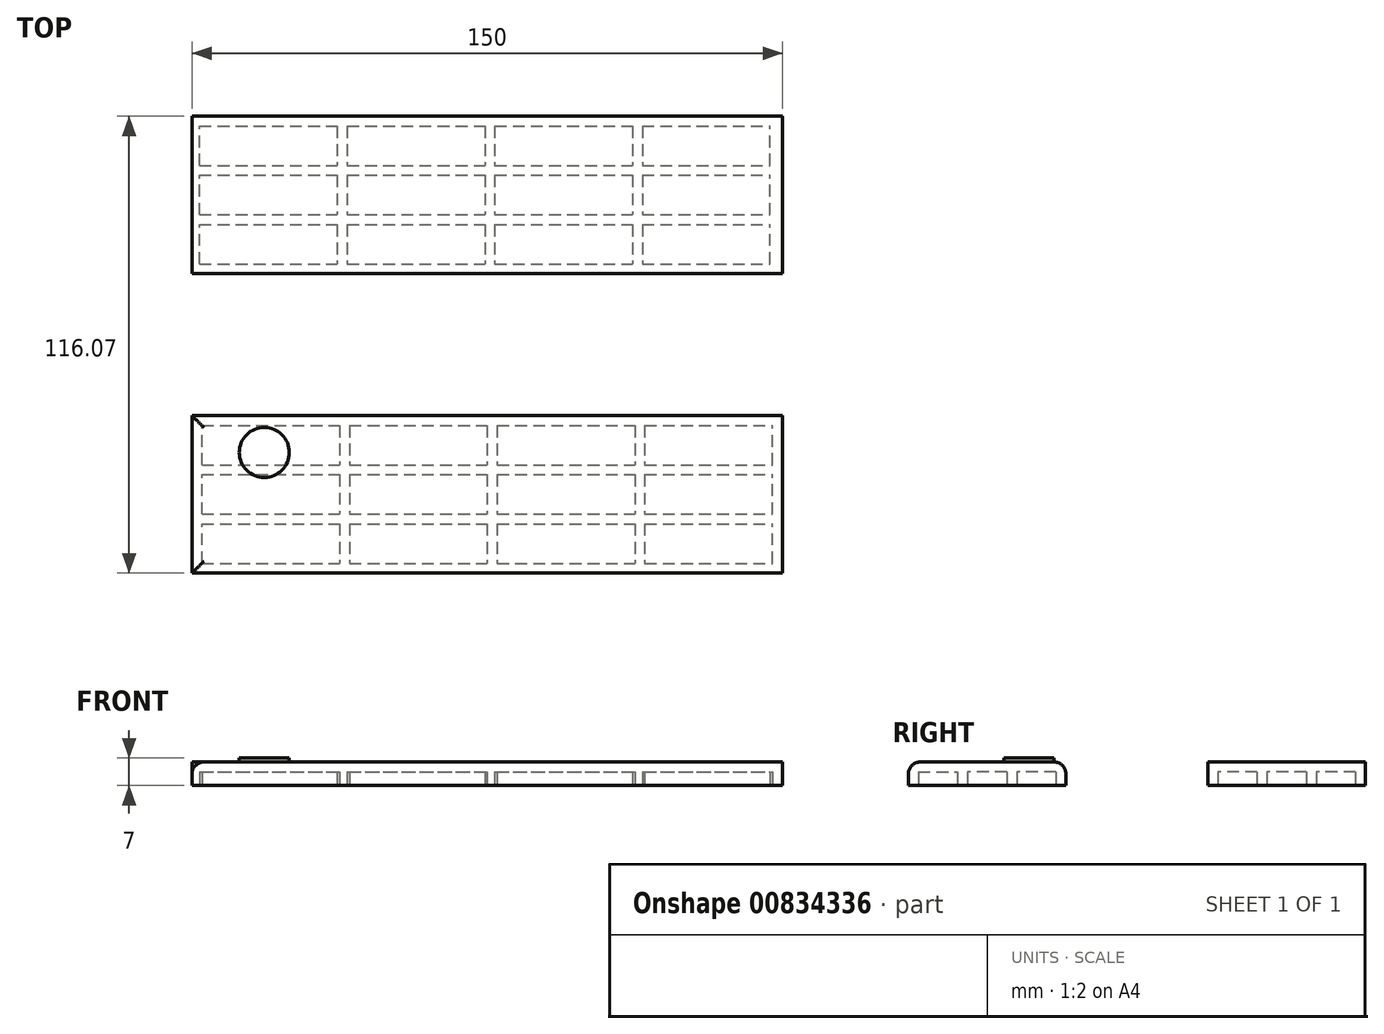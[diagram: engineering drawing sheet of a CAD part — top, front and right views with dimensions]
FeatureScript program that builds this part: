
annotation { "Feature Type Name" : "Feature", "Feature Type Description" : "" }
export const myFeature = defineFeature(function(context is Context, id is Id, definition is map)
    precondition{}
    {
        {
            var Q0;
            Q0=qCreatedBy(makeId("Top.planeOp"),FACE);
            var sketch = newSketch(context, id + "F0", { "sketchPlane" : qUnion([Q0])});
            skLineSegment(sketch, "E0.bottom", {"start": v(75, 20) * mm, "end": v(-75, 20) * mm});
            skLineSegment(sketch, "E0.top", {"start": v(75, -20) * mm, "end": v(-75, -20) * mm});
            skLineSegment(sketch, "E0.left", {"start": v(75, 20) * mm, "end": v(75, -20) * mm});
            skLineSegment(sketch, "E0.right", {"start": v(-75, 20) * mm, "end": v(-75, -20) * mm});
            skPoint(sketch, "E0.middle", {"position": v(0, 0) * mm});
            skSolve(sketch);
        }
        {
            var Q0;
            Q0 = qSketchRegion(id + "F0", true);
            extrude(context, id + "F1", {"entities" : qUnion([Q0]), "depth" : 6 * mm, "offsetDistance" : 25.4 * mm});
        }
        {
            var Q0;
            Q0=qCreatedBy(makeId("Top.planeOp"),FACE);
            var sketch = newSketch(context, id + "F2", { "sketchPlane" : qUnion([Q0])});
            skLineSegment(sketch, "E1.bottom", {"start": v(75, -56.07) * mm, "end": v(-75, -56.07) * mm});
            skLineSegment(sketch, "E1.top", {"start": v(75, -96.07) * mm, "end": v(-75, -96.07) * mm});
            skLineSegment(sketch, "E1.left", {"start": v(75, -56.07) * mm, "end": v(75, -96.07) * mm});
            skLineSegment(sketch, "E1.right", {"start": v(-75, -56.07) * mm, "end": v(-75, -96.07) * mm});
            skPoint(sketch, "E1.middle", {"position": v(0, -76.07) * mm});
            skSolve(sketch);
        }
        {
            var Q0;
            Q0 = qSketchRegion(id + "F2", true);
            extrude(context, id + "F3", {"entities" : qUnion([Q0]), "depth" : 6 * mm, "offsetDistance" : 25.4 * mm});
        }
        {
            var Q0;
            Q0=makeQuery(id+"F3.opExtrude","CAP_FACE",FACE,{"disambiguationData":[OSD([sQuery(id+"F2.wireOp",EDGE,"E1.bottom"),sQuery(id+"F2.wireOp",EDGE,"E1.top"),sQuery(id+"F2.wireOp",EDGE,"E1.left"),sQuery(id+"F2.wireOp",EDGE,"E1.right")])],"isStart":false});
            var sketch = newSketch(context, id + "F4", { "sketchPlane" : qUnion([Q0])});
            skCircle(sketch, "E2", {"center": v(-56.65, -65.42) * mm, "radius": 6.35 * mm});
            skSolve(sketch);
        }
        {
            var Q0;
            Q0 = qSketchRegion(id + "F4", true);
            extrude(context, id + "F5", {"entities" : qUnion([Q0]), "operationType" : NewBodyOperationType.ADD, "depth" : 1 * mm, "offsetDistance" : 25.4 * mm});
        }
        {
            var Q0;
            Q0=makeQuery(id+"F3.opExtrude","CAP_FACE",FACE,{"disambiguationData":[OSD([sQuery(id+"F2.wireOp",EDGE,"E1.bottom"),sQuery(id+"F2.wireOp",EDGE,"E1.top"),sQuery(id+"F2.wireOp",EDGE,"E1.left"),sQuery(id+"F2.wireOp",EDGE,"E1.right")])],"isStart":true});
            var sketch = newSketch(context, id + "F6", { "sketchPlane" : qUnion([Q0])});
            skLineSegment(sketch, "E3.bottom", {"start": v(-72.5, 93.57) * mm, "end": v(72.5, 93.57) * mm});
            skLineSegment(sketch, "E3.top", {"start": v(-72.5, 83.57) * mm, "end": v(72.5, 83.57) * mm});
            skLineSegment(sketch, "E3.left", {"start": v(-72.5, 93.57) * mm, "end": v(-72.5, 83.57) * mm});
            skLineSegment(sketch, "E3.right", {"start": v(72.5, 93.57) * mm, "end": v(72.5, 83.57) * mm});
            skLineSegment(sketch, "E4.bottom", {"start": v(-72.5, 81.07) * mm, "end": v(72.5, 81.07) * mm});
            skLineSegment(sketch, "E4.top", {"start": v(-72.5, 71.07) * mm, "end": v(72.5, 71.07) * mm});
            skLineSegment(sketch, "E4.left", {"start": v(-72.5, 81.07) * mm, "end": v(-72.5, 71.07) * mm});
            skLineSegment(sketch, "E4.right", {"start": v(72.5, 81.07) * mm, "end": v(72.5, 71.07) * mm});
            skLineSegment(sketch, "E5.bottom", {"start": v(-72.5, 68.57) * mm, "end": v(72.5, 68.57) * mm});
            skLineSegment(sketch, "E5.top", {"start": v(-72.5, 58.57) * mm, "end": v(72.5, 58.57) * mm});
            skLineSegment(sketch, "E5.left", {"start": v(-72.5, 68.57) * mm, "end": v(-72.5, 58.57) * mm});
            skLineSegment(sketch, "E5.right", {"start": v(72.5, 68.57) * mm, "end": v(72.5, 58.57) * mm});
            skLineSegment(sketch, "E6.bottom", {"start": v(-37.5, 58.57) * mm, "end": v(-35, 58.57) * mm});
            skLineSegment(sketch, "E6.top", {"start": v(-37.5, 93.57) * mm, "end": v(-35, 93.57) * mm});
            skLineSegment(sketch, "E6.left", {"start": v(-37.5, 58.57) * mm, "end": v(-37.5, 93.57) * mm});
            skLineSegment(sketch, "E6.right", {"start": v(-35, 58.57) * mm, "end": v(-35, 93.57) * mm});
            skLineSegment(sketch, "E7.bottom", {"start": v(0, 58.57) * mm, "end": v(2.5, 58.57) * mm});
            skLineSegment(sketch, "E7.top", {"start": v(0, 93.57) * mm, "end": v(2.5, 93.57) * mm});
            skLineSegment(sketch, "E7.left", {"start": v(0, 58.57) * mm, "end": v(0, 93.57) * mm});
            skLineSegment(sketch, "E7.right", {"start": v(2.5, 58.57) * mm, "end": v(2.5, 93.57) * mm});
            skLineSegment(sketch, "E8.bottom", {"start": v(37.5, 58.57) * mm, "end": v(40, 58.57) * mm});
            skLineSegment(sketch, "E8.top", {"start": v(37.5, 93.57) * mm, "end": v(40, 93.57) * mm});
            skLineSegment(sketch, "E8.left", {"start": v(37.5, 58.57) * mm, "end": v(37.5, 93.57) * mm});
            skLineSegment(sketch, "E8.right", {"start": v(40, 58.57) * mm, "end": v(40, 93.57) * mm});
            skSolve(sketch);
        }
        {
            var Q0;
            {var subQ0=sQuery(id+"F6.wireOp",EDGE,"E3.left");Q0=makeQuery(id+"F6.imprint","IMPRINT",FACE,{"disambiguationData":[TD([[makeQuery(id+"F6.imprint","IMPRINT",EDGE,{"derivedFrom":subQ0}),1.0]])]});}
            var Q1;
            {var subQ0=sQuery(id+"F6.wireOp",EDGE,"E6.right");var subQ5=sQuery(id+"F6.wireOp",EDGE,"E3.top");var subQ6=makeQuery(id+"F6.imprint","INTERSECT",VERTEX,{"derivedFrom":[subQ5,subQ0]});Q1=makeQuery(id+"F6.imprint","IMPRINT",FACE,{"disambiguationData":[TD([[makeQuery(id+"F6.imprint","IMPRINT",EDGE,{"disambiguationData":[TD([[subQ6,-1.0]])],"derivedFrom":subQ5}),1.0]])]});}
            var Q2;
            {var subQ0=sQuery(id+"F6.wireOp",EDGE,"E6.right");var subQ1=sQuery(id+"F6.wireOp",EDGE,"E4.bottom");var subQ2=makeQuery(id+"F6.imprint","INTERSECT",VERTEX,{"derivedFrom":[subQ1,subQ0]});Q2=makeQuery(id+"F6.imprint","IMPRINT",FACE,{"disambiguationData":[TD([[makeQuery(id+"F6.imprint","IMPRINT",EDGE,{"disambiguationData":[TD([[subQ2,-1.0]])],"derivedFrom":subQ1}),-1.0]])]});}
            var Q3;
            {var subQ0=sQuery(id+"F6.wireOp",EDGE,"E4.left");Q3=makeQuery(id+"F6.imprint","IMPRINT",FACE,{"disambiguationData":[TD([[makeQuery(id+"F6.imprint","IMPRINT",EDGE,{"derivedFrom":subQ0}),1.0]])]});}
            var Q4;
            {var subQ0=sQuery(id+"F6.wireOp",EDGE,"E5.left");Q4=makeQuery(id+"F6.imprint","IMPRINT",FACE,{"disambiguationData":[TD([[makeQuery(id+"F6.imprint","IMPRINT",EDGE,{"derivedFrom":subQ0}),1.0]])]});}
            var Q5;
            {var subQ0=sQuery(id+"F6.wireOp",EDGE,"E7.right");var subQ1=sQuery(id+"F6.wireOp",EDGE,"E5.bottom");var subQ2=makeQuery(id+"F6.imprint","INTERSECT",VERTEX,{"derivedFrom":[subQ1,subQ0]});Q5=makeQuery(id+"F6.imprint","IMPRINT",FACE,{"disambiguationData":[TD([[makeQuery(id+"F6.imprint","IMPRINT",EDGE,{"disambiguationData":[TD([[subQ2,-1.0]])],"derivedFrom":subQ1}),-1.0]])]});}
            var Q6;
            {var subQ0=sQuery(id+"F6.wireOp",EDGE,"E7.right");var subQ1=sQuery(id+"F6.wireOp",EDGE,"E4.bottom");var subQ2=makeQuery(id+"F6.imprint","INTERSECT",VERTEX,{"derivedFrom":[subQ1,subQ0]});Q6=makeQuery(id+"F6.imprint","IMPRINT",FACE,{"disambiguationData":[TD([[makeQuery(id+"F6.imprint","IMPRINT",EDGE,{"disambiguationData":[TD([[subQ2,-1.0]])],"derivedFrom":subQ1}),-1.0]])]});}
            var Q7;
            {var subQ0=sQuery(id+"F6.wireOp",EDGE,"E7.right");var subQ5=sQuery(id+"F6.wireOp",EDGE,"E3.top");var subQ7=makeQuery(id+"F6.imprint","INTERSECT",VERTEX,{"derivedFrom":[subQ5,subQ0]});Q7=makeQuery(id+"F6.imprint","IMPRINT",FACE,{"disambiguationData":[TD([[makeQuery(id+"F6.imprint","IMPRINT",EDGE,{"disambiguationData":[TD([[subQ7,-1.0]])],"derivedFrom":subQ5}),1.0]])]});}
            var Q8;
            {var subQ0=sQuery(id+"F6.wireOp",EDGE,"E6.right");var subQ1=sQuery(id+"F6.wireOp",EDGE,"E5.bottom");var subQ2=makeQuery(id+"F6.imprint","INTERSECT",VERTEX,{"derivedFrom":[subQ1,subQ0]});Q8=makeQuery(id+"F6.imprint","IMPRINT",FACE,{"disambiguationData":[TD([[makeQuery(id+"F6.imprint","IMPRINT",EDGE,{"disambiguationData":[TD([[subQ2,-1.0]])],"derivedFrom":subQ1}),-1.0]])]});}
            var Q9;
            {var subQ0=sQuery(id+"F6.wireOp",EDGE,"E3.right");Q9=makeQuery(id+"F6.imprint","IMPRINT",FACE,{"disambiguationData":[TD([[makeQuery(id+"F6.imprint","IMPRINT",EDGE,{"derivedFrom":subQ0}),-1.0]])]});}
            var Q10;
            {var subQ0=sQuery(id+"F6.wireOp",EDGE,"E4.right");Q10=makeQuery(id+"F6.imprint","IMPRINT",FACE,{"disambiguationData":[TD([[makeQuery(id+"F6.imprint","IMPRINT",EDGE,{"derivedFrom":subQ0}),-1.0]])]});}
            var Q11;
            {var subQ0=sQuery(id+"F6.wireOp",EDGE,"E5.right");Q11=makeQuery(id+"F6.imprint","IMPRINT",FACE,{"disambiguationData":[TD([[makeQuery(id+"F6.imprint","IMPRINT",EDGE,{"derivedFrom":subQ0}),-1.0]])]});}
            extrude(context, id + "F7", {"entities" : qUnion([Q0, Q1, Q2, Q3, Q4, Q5, Q6, Q7, Q8, Q9, Q10, Q11]), "operationType" : NewBodyOperationType.REMOVE, "oppositeDirection" : true, "depth" : 3.5 * mm, "offsetDistance" : 25.4 * mm});
        }
        {
            var Q0;
            Q0=makeQuery(id+"F3.opExtrude","CAP_EDGE",EDGE,{"disambiguationData":[OSD([sQuery(id+"F2.wireOp",EDGE,"E1.bottom")])],"isStart":false});
            var Q1;
            Q1=makeQuery(id+"F3.opExtrude","CAP_EDGE",EDGE,{"disambiguationData":[OSD([sQuery(id+"F2.wireOp",EDGE,"E1.right")])],"isStart":false});
            var Q2;
            Q2=makeQuery(id+"F3.opExtrude","CAP_EDGE",EDGE,{"disambiguationData":[OSD([sQuery(id+"F2.wireOp",EDGE,"E1.top")])],"isStart":false});
            fillet(context, id + "F8", {"entities" : qUnion([Q0, Q1, Q2]), "radius" : 3 * mm, "tangentPropagation" : true, "allowEdgeOverflow" : false});
        }
        {
            var Q0;
            Q0=makeQuery(id+"F1.opExtrude","CAP_FACE",FACE,{"disambiguationData":[OSD([sQuery(id+"F0.wireOp",EDGE,"E0.bottom"),sQuery(id+"F0.wireOp",EDGE,"E0.top"),sQuery(id+"F0.wireOp",EDGE,"E0.left"),sQuery(id+"F0.wireOp",EDGE,"E0.right")])],"isStart":true});
            var sketch = newSketch(context, id + "F9", { "sketchPlane" : qUnion([Q0])});
            skLineSegment(sketch, "E9.bottom", {"start": v(-73.12, 17.5) * mm, "end": v(71.88, 17.5) * mm});
            skLineSegment(sketch, "E9.top", {"start": v(-73.12, 7.5) * mm, "end": v(71.88, 7.5) * mm});
            skLineSegment(sketch, "E9.left", {"start": v(-73.12, 17.5) * mm, "end": v(-73.12, 7.5) * mm});
            skLineSegment(sketch, "E9.right", {"start": v(71.88, 17.5) * mm, "end": v(71.88, 7.5) * mm});
            skLineSegment(sketch, "E10.bottom", {"start": v(-73.12, 5) * mm, "end": v(71.88, 5) * mm});
            skLineSegment(sketch, "E10.top", {"start": v(-73.12, -5) * mm, "end": v(71.88, -5) * mm});
            skLineSegment(sketch, "E10.left", {"start": v(-73.12, 5) * mm, "end": v(-73.12, -5) * mm});
            skLineSegment(sketch, "E10.right", {"start": v(71.88, 5) * mm, "end": v(71.88, -5) * mm});
            skLineSegment(sketch, "E11.bottom", {"start": v(-73.12, -7.5) * mm, "end": v(71.88, -7.5) * mm});
            skLineSegment(sketch, "E11.top", {"start": v(-73.12, -17.5) * mm, "end": v(71.88, -17.5) * mm});
            skLineSegment(sketch, "E11.left", {"start": v(-73.12, -7.5) * mm, "end": v(-73.12, -17.5) * mm});
            skLineSegment(sketch, "E11.right", {"start": v(71.88, -7.5) * mm, "end": v(71.88, -17.5) * mm});
            skLineSegment(sketch, "E12.bottom", {"start": v(-38.12, -17.5) * mm, "end": v(-35.62, -17.5) * mm});
            skLineSegment(sketch, "E12.top", {"start": v(-38.12, 17.5) * mm, "end": v(-35.62, 17.5) * mm});
            skLineSegment(sketch, "E12.left", {"start": v(-38.12, -17.5) * mm, "end": v(-38.12, 17.5) * mm});
            skLineSegment(sketch, "E12.right", {"start": v(-35.62, -17.5) * mm, "end": v(-35.62, 17.5) * mm});
            skLineSegment(sketch, "E13.bottom", {"start": v(-0.62, -17.5) * mm, "end": v(1.88, -17.5) * mm});
            skLineSegment(sketch, "E13.top", {"start": v(-0.62, 17.5) * mm, "end": v(1.88, 17.5) * mm});
            skLineSegment(sketch, "E13.left", {"start": v(-0.62, -17.5) * mm, "end": v(-0.62, 17.5) * mm});
            skLineSegment(sketch, "E13.right", {"start": v(1.88, -17.5) * mm, "end": v(1.88, 17.5) * mm});
            skLineSegment(sketch, "E14.bottom", {"start": v(36.88, -17.5) * mm, "end": v(39.38, -17.5) * mm});
            skLineSegment(sketch, "E14.top", {"start": v(36.88, 17.5) * mm, "end": v(39.38, 17.5) * mm});
            skLineSegment(sketch, "E14.left", {"start": v(36.88, -17.5) * mm, "end": v(36.88, 17.5) * mm});
            skLineSegment(sketch, "E14.right", {"start": v(39.38, -17.5) * mm, "end": v(39.38, 17.5) * mm});
            skSolve(sketch);
        }
        {
            var Q0;
            {var subQ0=sQuery(id+"F9.wireOp",EDGE,"E11.right");Q0=makeQuery(id+"F9.imprint","IMPRINT",FACE,{"disambiguationData":[TD([[makeQuery(id+"F9.imprint","IMPRINT",EDGE,{"derivedFrom":subQ0}),-1.0]])]});}
            var Q1;
            {var subQ0=sQuery(id+"F9.wireOp",EDGE,"E13.right");var subQ1=sQuery(id+"F9.wireOp",EDGE,"E11.bottom");var subQ2=makeQuery(id+"F9.imprint","INTERSECT",VERTEX,{"derivedFrom":[subQ1,subQ0]});Q1=makeQuery(id+"F9.imprint","IMPRINT",FACE,{"disambiguationData":[TD([[makeQuery(id+"F9.imprint","IMPRINT",EDGE,{"disambiguationData":[TD([[subQ2,-1.0]])],"derivedFrom":subQ1}),-1.0]])]});}
            var Q2;
            {var subQ0=sQuery(id+"F9.wireOp",EDGE,"E10.right");Q2=makeQuery(id+"F9.imprint","IMPRINT",FACE,{"disambiguationData":[TD([[makeQuery(id+"F9.imprint","IMPRINT",EDGE,{"derivedFrom":subQ0}),-1.0]])]});}
            var Q3;
            {var subQ0=sQuery(id+"F9.wireOp",EDGE,"E13.right");var subQ1=sQuery(id+"F9.wireOp",EDGE,"E10.bottom");var subQ2=makeQuery(id+"F9.imprint","INTERSECT",VERTEX,{"derivedFrom":[subQ1,subQ0]});Q3=makeQuery(id+"F9.imprint","IMPRINT",FACE,{"disambiguationData":[TD([[makeQuery(id+"F9.imprint","IMPRINT",EDGE,{"disambiguationData":[TD([[subQ2,-1.0]])],"derivedFrom":subQ1}),-1.0]])]});}
            var Q4;
            {var subQ0=sQuery(id+"F9.wireOp",EDGE,"E9.right");Q4=makeQuery(id+"F9.imprint","IMPRINT",FACE,{"disambiguationData":[TD([[makeQuery(id+"F9.imprint","IMPRINT",EDGE,{"derivedFrom":subQ0}),-1.0]])]});}
            var Q5;
            {var subQ0=sQuery(id+"F9.wireOp",EDGE,"E12.right");var subQ1=sQuery(id+"F9.wireOp",EDGE,"E11.bottom");var subQ2=makeQuery(id+"F9.imprint","INTERSECT",VERTEX,{"derivedFrom":[subQ1,subQ0]});Q5=makeQuery(id+"F9.imprint","IMPRINT",FACE,{"disambiguationData":[TD([[makeQuery(id+"F9.imprint","IMPRINT",EDGE,{"disambiguationData":[TD([[subQ2,-1.0]])],"derivedFrom":subQ1}),-1.0]])]});}
            var Q6;
            {var subQ0=sQuery(id+"F9.wireOp",EDGE,"E11.left");Q6=makeQuery(id+"F9.imprint","IMPRINT",FACE,{"disambiguationData":[TD([[makeQuery(id+"F9.imprint","IMPRINT",EDGE,{"derivedFrom":subQ0}),1.0]])]});}
            var Q7;
            {var subQ0=sQuery(id+"F9.wireOp",EDGE,"E10.left");Q7=makeQuery(id+"F9.imprint","IMPRINT",FACE,{"disambiguationData":[TD([[makeQuery(id+"F9.imprint","IMPRINT",EDGE,{"derivedFrom":subQ0}),1.0]])]});}
            var Q8;
            {var subQ0=sQuery(id+"F9.wireOp",EDGE,"E9.left");Q8=makeQuery(id+"F9.imprint","IMPRINT",FACE,{"disambiguationData":[TD([[makeQuery(id+"F9.imprint","IMPRINT",EDGE,{"derivedFrom":subQ0}),1.0]])]});}
            var Q9;
            {var subQ0=sQuery(id+"F9.wireOp",EDGE,"E12.right");var subQ5=sQuery(id+"F9.wireOp",EDGE,"E9.top");var subQ6=makeQuery(id+"F9.imprint","INTERSECT",VERTEX,{"derivedFrom":[subQ5,subQ0]});Q9=makeQuery(id+"F9.imprint","IMPRINT",FACE,{"disambiguationData":[TD([[makeQuery(id+"F9.imprint","IMPRINT",EDGE,{"disambiguationData":[TD([[subQ6,-1.0]])],"derivedFrom":subQ5}),1.0]])]});}
            var Q10;
            {var subQ0=sQuery(id+"F9.wireOp",EDGE,"E12.right");var subQ1=sQuery(id+"F9.wireOp",EDGE,"E10.bottom");var subQ2=makeQuery(id+"F9.imprint","INTERSECT",VERTEX,{"derivedFrom":[subQ1,subQ0]});Q10=makeQuery(id+"F9.imprint","IMPRINT",FACE,{"disambiguationData":[TD([[makeQuery(id+"F9.imprint","IMPRINT",EDGE,{"disambiguationData":[TD([[subQ2,-1.0]])],"derivedFrom":subQ1}),-1.0]])]});}
            var Q11;
            {var subQ0=sQuery(id+"F9.wireOp",EDGE,"E13.right");var subQ5=sQuery(id+"F9.wireOp",EDGE,"E9.top");var subQ7=makeQuery(id+"F9.imprint","INTERSECT",VERTEX,{"derivedFrom":[subQ5,subQ0]});Q11=makeQuery(id+"F9.imprint","IMPRINT",FACE,{"disambiguationData":[TD([[makeQuery(id+"F9.imprint","IMPRINT",EDGE,{"disambiguationData":[TD([[subQ7,-1.0]])],"derivedFrom":subQ5}),1.0]])]});}
            extrude(context, id + "F10", {"entities" : qUnion([Q0, Q1, Q2, Q3, Q4, Q5, Q6, Q7, Q8, Q9, Q10, Q11]), "operationType" : NewBodyOperationType.REMOVE, "oppositeDirection" : true, "depth" : 3.5 * mm, "offsetDistance" : 25.4 * mm});
        }
    });
